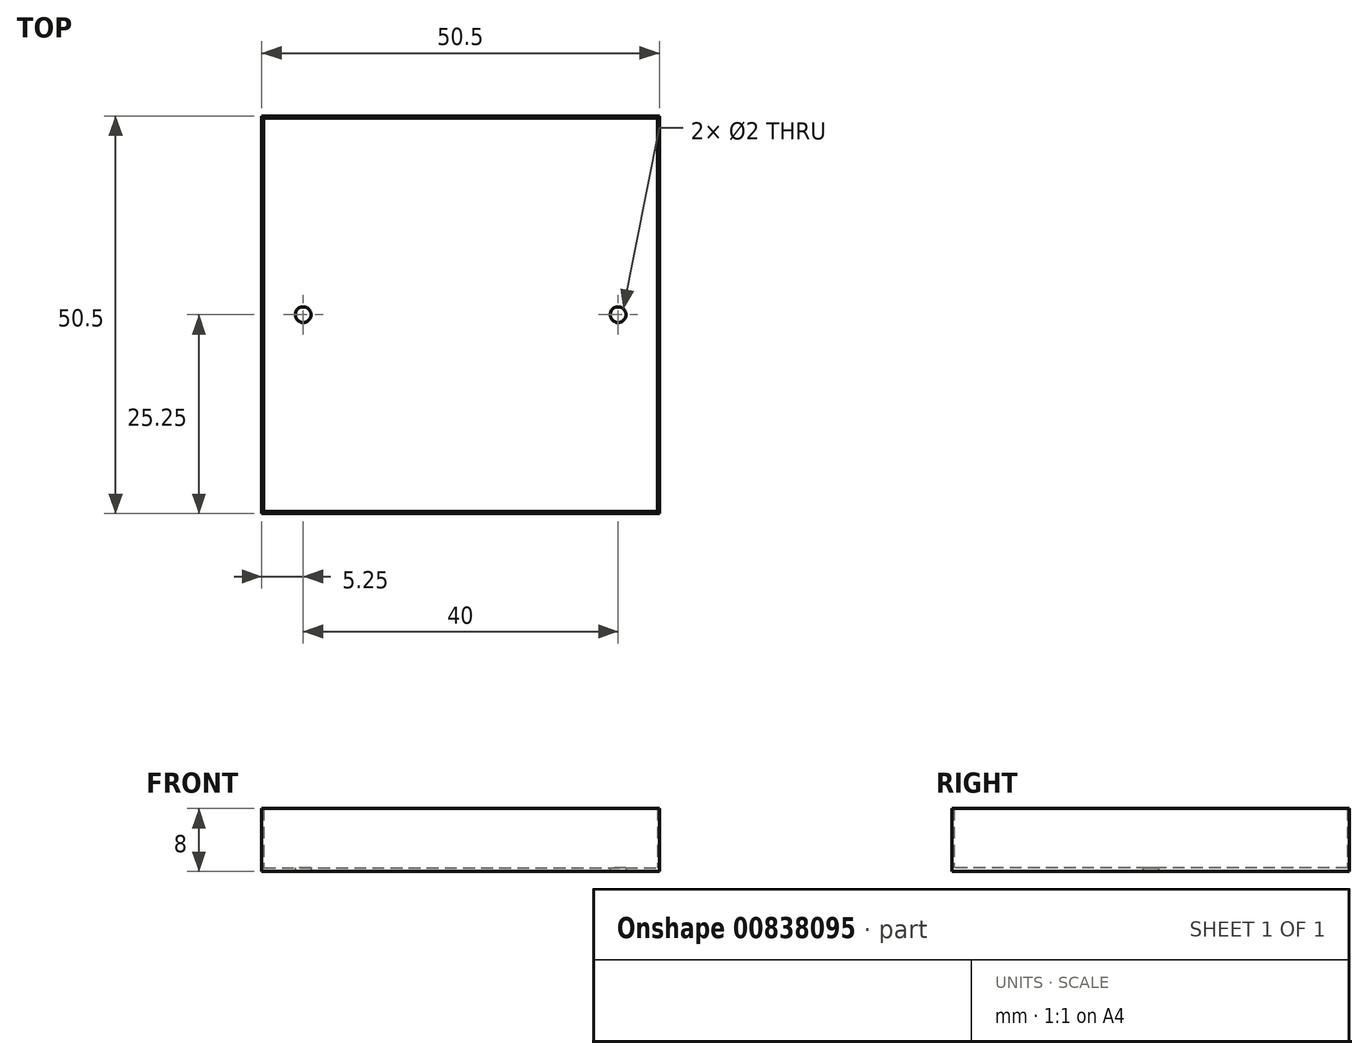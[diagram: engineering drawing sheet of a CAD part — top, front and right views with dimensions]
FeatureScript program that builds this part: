
annotation { "Feature Type Name" : "Feature", "Feature Type Description" : "" }
export const myFeature = defineFeature(function(context is Context, id is Id, definition is map)
    precondition{}
    {
        {
            var Q0;
            Q0=qCreatedBy(makeId("Top.planeOp"),FACE);
            var sketch = newSketch(context, id + "F0", { "sketchPlane" : qUnion([Q0])});
            skLineSegment(sketch, "E0.bottom", {"start": v(-25, 25) * mm, "end": v(25, 25) * mm});
            skLineSegment(sketch, "E0.top", {"start": v(-25, -25) * mm, "end": v(25, -25) * mm});
            skLineSegment(sketch, "E0.left", {"start": v(-25, 25) * mm, "end": v(-25, -25) * mm});
            skLineSegment(sketch, "E0.right", {"start": v(25, 25) * mm, "end": v(25, -25) * mm});
            skPoint(sketch, "E0.middle", {"position": v(0, 0) * mm});
            skLineSegment(sketch, "E1", {"start": v(0, 0) * mm, "end": v(-25, 0) * mm});
            skLineSegment(sketch, "E2", {"start": v(0, 0) * mm, "end": v(25, 0) * mm});
            skCircle(sketch, "E3", {"center": v(-20, 0) * mm, "radius": 1 * mm});
            skCircle(sketch, "E4", {"center": v(20, 0) * mm, "radius": 1 * mm});
            skLineSegment(sketch, "E5.bottom", {"start": v(-25.25, 25.25) * mm, "end": v(25.25, 25.25) * mm});
            skLineSegment(sketch, "E5.top", {"start": v(-25.25, -25.25) * mm, "end": v(25.25, -25.25) * mm});
            skLineSegment(sketch, "E5.left", {"start": v(-25.25, 25.25) * mm, "end": v(-25.25, -25.25) * mm});
            skLineSegment(sketch, "E5.right", {"start": v(25.25, 25.25) * mm, "end": v(25.25, -25.25) * mm});
            skSolve(sketch);
        }
        {
            var Q0;
            {var subQ3=sQuery(id+"F0.wireOp",EDGE,"E0.bottom");Q0=makeQuery(id+"F0.imprint","IMPRINT",FACE,{"disambiguationData":[TD([[makeQuery(id+"F0.imprint","IMPRINT",EDGE,{"derivedFrom":subQ3}),1.0]])]});}
            extrude(context, id + "F1", {"entities" : qUnion([Q0]), "depth" : 8 * mm, "offsetDistance" : 25 * mm});
        }
        {
            var Q0;
            {var subQ6=sQuery(id+"F0.wireOp",EDGE,"E0.bottom");Q0=makeQuery(id+"F0.imprint","IMPRINT",FACE,{"disambiguationData":[TD([[makeQuery(id+"F0.imprint","IMPRINT",EDGE,{"derivedFrom":subQ6}),-1.0]])]});}
            var Q1;
            {var subQ1=sQuery(id+"F0.wireOp",EDGE,"E0.top");Q1=makeQuery(id+"F0.imprint","IMPRINT",FACE,{"disambiguationData":[TD([[makeQuery(id+"F0.imprint","IMPRINT",EDGE,{"derivedFrom":subQ1}),1.0]])]});}
            extrude(context, id + "F2", {"entities" : qUnion([Q0, Q1]), "operationType" : NewBodyOperationType.ADD, "depth" : 0.5 * mm, "offsetDistance" : 25 * mm});
        }
    });
